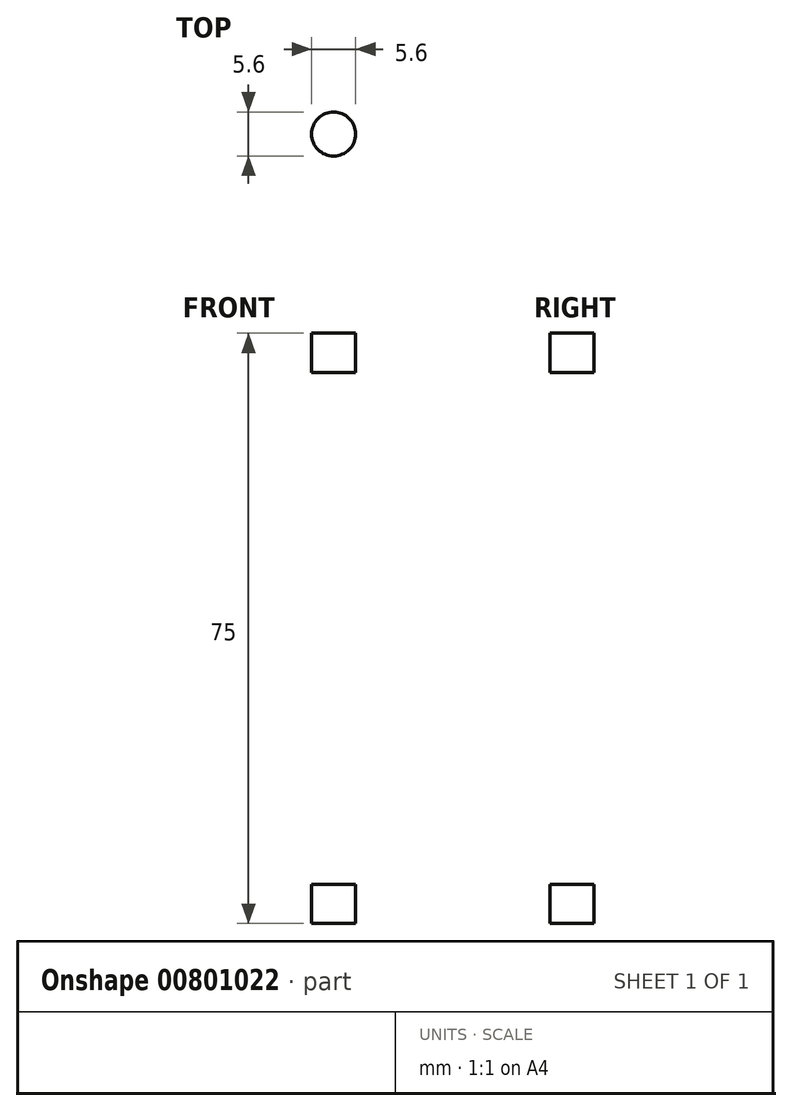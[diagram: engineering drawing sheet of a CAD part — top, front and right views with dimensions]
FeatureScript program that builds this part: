
annotation { "Feature Type Name" : "Feature", "Feature Type Description" : "" }
export const myFeature = defineFeature(function(context is Context, id is Id, definition is map)
    precondition{}
    {
        {
            var Q0;
            Q0=qCreatedBy(makeId("Top.planeOp"),FACE);
            var sketch = newSketch(context, id + "F0", { "sketchPlane" : qUnion([Q0])});
            skLineSegment(sketch, "E0.bottom", {"start": v(-35.86, 6.14) * mm, "end": v(35.86, 6.14) * mm});
            skLineSegment(sketch, "E0.top", {"start": v(-35.86, -6.14) * mm, "end": v(35.86, -6.14) * mm});
            skLineSegment(sketch, "E0.left", {"start": v(-35.86, 6.14) * mm, "end": v(-35.86, -6.14) * mm});
            skLineSegment(sketch, "E0.right", {"start": v(35.86, 6.14) * mm, "end": v(35.86, -6.14) * mm});
            skLineSegment(sketch, "E1", {"start": v(0, 0) * mm, "end": v(0, 6.14) * mm, "construction": true});
            skLineSegment(sketch, "E2", {"start": v(-35.86, 0) * mm, "end": v(0, 0) * mm, "construction": true});
            skSolve(sketch);
        }
        {
            var Q0;
            Q0=makeQuery(id+"F0.imprint","IMPRINT",FACE,{"disambiguationData":[TD([[makeQuery(id+"F0.imprint","IMPRINT",EDGE,{"derivedFrom":sQuery(id+"F0.wireOp",EDGE,"E0.bottom")}),-1.0]])]});
            extrude(context, id + "F1", {"entities" : qUnion([Q0]), "endBound" : BoundingType.SYMMETRIC, "depth" : 75 * mm, "offsetDistance" : 25 * mm});
        }
        {
            var Q0;
            Q0=makeQuery(id+"F1.opExtrude","SWEPT_FACE",FACE,{"disambiguationData":[OSD([sQuery(id+"F0.wireOp",EDGE,"E0.bottom")])]});
            var sketch = newSketch(context, id + "F2", { "sketchPlane" : qUnion([Q0])});
            skLineSegment(sketch, "E3.bottom", {"start": v(-35.86, 32.5) * mm, "end": v(-5.86, 32.5) * mm});
            skLineSegment(sketch, "E3.top", {"start": v(-35.86, -32.5) * mm, "end": v(-5.86, -32.5) * mm});
            skLineSegment(sketch, "E3.left", {"start": v(-35.86, 32.5) * mm, "end": v(-35.86, -32.5) * mm});
            skLineSegment(sketch, "E3.right", {"start": v(-5.86, 32.5) * mm, "end": v(-5.86, -32.5) * mm});
            skLineSegment(sketch, "E4.MirrorCS", {"start": v(35.86, 32.5) * mm, "end": v(5.86, 32.5) * mm});
            skLineSegment(sketch, "E5.MirrorCS", {"start": v(5.86, 32.5) * mm, "end": v(5.86, -32.5) * mm});
            skLineSegment(sketch, "E6.MirrorCS", {"start": v(35.86, -32.5) * mm, "end": v(5.86, -32.5) * mm});
            skSolve(sketch);
        }
        {
            var Q0;
            Q0=makeQuery(id+"F2.imprint","IMPRINT",FACE,{"disambiguationData":[TD([[makeQuery(id+"F2.imprint","IMPRINT",EDGE,{"derivedFrom":sQuery(id+"F2.wireOp",EDGE,"E3.bottom")}),-1.0]])]});
            var Q1;
            {var subQ0=sQuery(id+"F2.wireOp",EDGE,"E4.MirrorCS");Q1=makeQuery(id+"F2.imprint","IMPRINT",FACE,{"disambiguationData":[TD([[makeQuery(id+"F2.imprint","IMPRINT",EDGE,{"derivedFrom":subQ0}),1.0]])]});}
            extrude(context, id + "F3", {"entities" : qUnion([Q0, Q1]), "operationType" : NewBodyOperationType.REMOVE, "endBound" : BoundingType.THROUGH_ALL, "oppositeDirection" : true, "depth" : 25 * mm, "offsetDistance" : 25 * mm});
        }
        {
            var Q0;
            Q0=makeQuery(id+"F1.opExtrude","CAP_FACE",FACE,{"disambiguationData":[OSD([sQuery(id+"F0.wireOp",EDGE,"E0.bottom"),sQuery(id+"F0.wireOp",EDGE,"E0.top"),sQuery(id+"F0.wireOp",EDGE,"E0.left"),sQuery(id+"F0.wireOp",EDGE,"E0.right")])],"isStart":false});
            var sketch = newSketch(context, id + "F4", { "sketchPlane" : qUnion([Q0])});
            skCircle(sketch, "E7", {"center": v(-29.86, 0) * mm, "radius": 2.8 * mm});
            skCircle(sketch, "E8.MirrorC", {"center": v(29.86, 0) * mm, "radius": 2.8 * mm});
            skSolve(sketch);
        }
        {
            var Q0;
            Q0=makeQuery(id+"F4.imprint","IMPRINT",FACE,{"disambiguationData":[TD([[makeQuery(id+"F4.imprint","IMPRINT",EDGE,{"derivedFrom":sQuery(id+"F4.wireOp",EDGE,"E7")}),1.0]])]});
            var Q1;
            Q1=makeQuery(id+"F4.imprint","IMPRINT",FACE,{"disambiguationData":[TD([[makeQuery(id+"F4.imprint","IMPRINT",EDGE,{"derivedFrom":sQuery(id+"F4.wireOp",EDGE,"E8.MirrorC")}),-1.0]])]});
            extrude(context, id + "F5", {"entities" : qUnion([Q0, Q1]), "operationType" : NewBodyOperationType.REMOVE, "endBound" : BoundingType.THROUGH_ALL, "oppositeDirection" : true, "depth" : 25 * mm, "offsetDistance" : 25 * mm});
        }
    });
